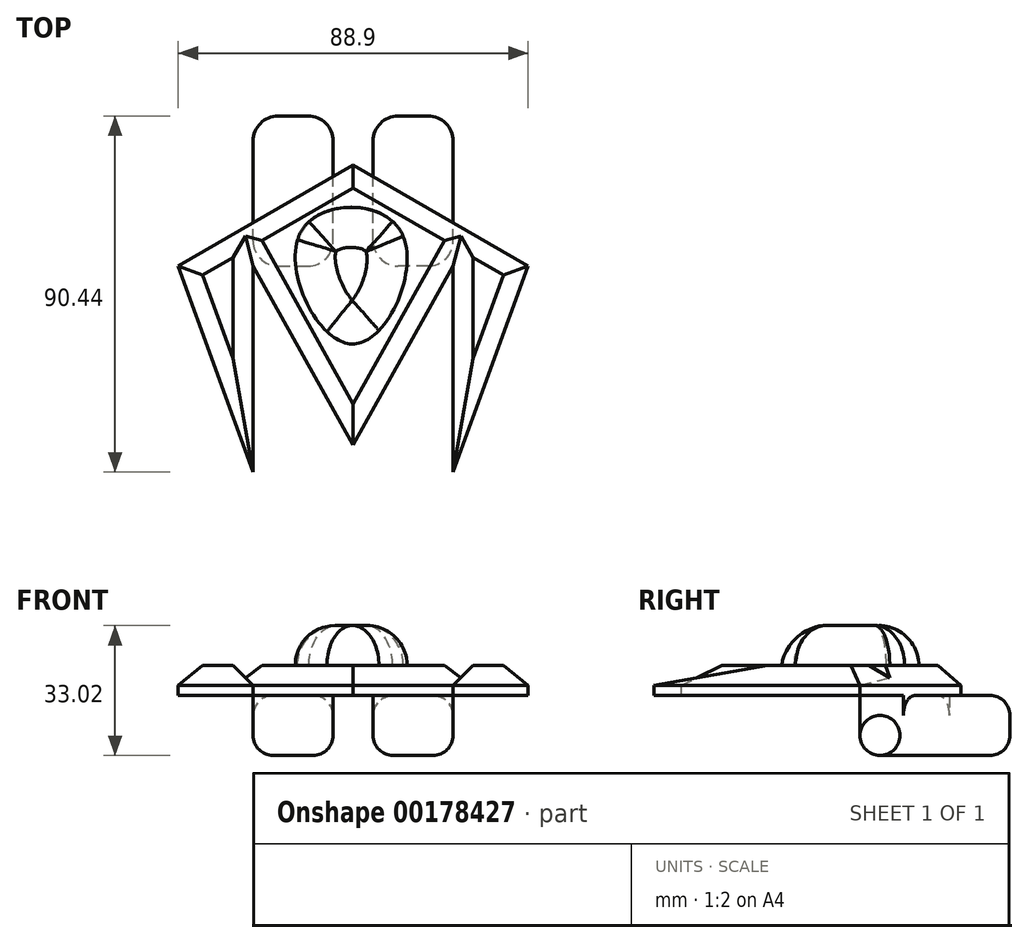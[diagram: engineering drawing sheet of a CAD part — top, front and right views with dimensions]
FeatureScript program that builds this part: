
annotation { "Feature Type Name" : "Feature", "Feature Type Description" : "" }
export const myFeature = defineFeature(function(context is Context, id is Id, definition is map)
    precondition{}
    {
        {
            var Q0;
            Q0=qCreatedBy(makeId("Top.planeOp"),FACE);
            var sketch = newSketch(context, id + "F0", { "sketchPlane" : qUnion([Q0])});
            skLineSegment(sketch, "E0", {"start": v(-25.4, 8.08) * mm, "end": v(0, -37.38) * mm});
            skLineSegment(sketch, "E1", {"start": v(0, -37.38) * mm, "end": v(25.4, 8.08) * mm});
            skLineSegment(sketch, "E2", {"start": v(25.4, 8.08) * mm, "end": v(25.4, -44.26) * mm});
            skLineSegment(sketch, "E3", {"start": v(-25.4, 8.08) * mm, "end": v(-25.4, -44.26) * mm});
            skLineSegment(sketch, "E4", {"start": v(-25.4, -44.26) * mm, "end": v(-44.45, 8.08) * mm});
            skLineSegment(sketch, "E5", {"start": v(25.4, -44.26) * mm, "end": v(44.45, 8.08) * mm});
            skLineSegment(sketch, "E6", {"start": v(0, -37.38) * mm, "end": v(0, 33.74) * mm});
            skLineSegment(sketch, "E7", {"start": v(0, 33.74) * mm, "end": v(44.45, 8.08) * mm});
            skLineSegment(sketch, "E8", {"start": v(0, 33.74) * mm, "end": v(-44.45, 8.08) * mm});
            skSolve(sketch);
        }
        {
            var Q0;
            Q0 = qSketchRegion(id + "F0", true);
            extrude(context, id + "F1", {"entities" : qUnion([Q0]), "depth" : 7.62 * mm});
        }
        {
            var Q0;
            Q0=makeQuery(id+"F1.opExtrude","CAP_FACE",FACE,{"disambiguationData":[OSD([sQuery(id+"F0.wireOp",EDGE,"E0"),sQuery(id+"F0.wireOp",EDGE,"E1"),sQuery(id+"F0.wireOp",EDGE,"E2"),sQuery(id+"F0.wireOp",EDGE,"E3"),sQuery(id+"F0.wireOp",EDGE,"E4"),sQuery(id+"F0.wireOp",EDGE,"E5"),sQuery(id+"F0.wireOp",EDGE,"E7"),sQuery(id+"F0.wireOp",EDGE,"E8")])],"isStart":false});
            chamfer(context, id + "F2", {"entities" : qUnion([Q0]), "width" : 5.08 * mm, "tangentPropagation" : true});
        }
        {
            var Q0;
            Q0=makeQuery(id+"F1.opExtrude","CAP_FACE",FACE,{"disambiguationData":[OSD([sQuery(id+"F0.wireOp",EDGE,"E0"),sQuery(id+"F0.wireOp",EDGE,"E1"),sQuery(id+"F0.wireOp",EDGE,"E2"),sQuery(id+"F0.wireOp",EDGE,"E3"),sQuery(id+"F0.wireOp",EDGE,"E4"),sQuery(id+"F0.wireOp",EDGE,"E5"),sQuery(id+"F0.wireOp",EDGE,"E7"),sQuery(id+"F0.wireOp",EDGE,"E8")])],"isStart":true});
            var sketch = newSketch(context, id + "F3", { "sketchPlane" : qUnion([Q0])});
            skLineSegment(sketch, "E9.bottom", {"start": v(-19.05, -8.08) * mm, "end": v(-11.43, -8.08) * mm});
            skLineSegment(sketch, "E9.top", {"start": v(-19.05, -46.18) * mm, "end": v(-11.43, -46.18) * mm});
            skLineSegment(sketch, "E9.left", {"start": v(-25.4, -14.43) * mm, "end": v(-25.4, -39.83) * mm});
            skLineSegment(sketch, "E9.right", {"start": v(-5.08, -14.43) * mm, "end": v(-5.08, -39.83) * mm});
            skLineSegment(sketch, "E10.bottom", {"start": v(19.05, -8.08) * mm, "end": v(11.43, -8.08) * mm});
            skLineSegment(sketch, "E10.top", {"start": v(19.05, -46.18) * mm, "end": v(11.43, -46.18) * mm});
            skLineSegment(sketch, "E10.left", {"start": v(25.4, -14.43) * mm, "end": v(25.4, -39.83) * mm});
            skLineSegment(sketch, "E10.right", {"start": v(5.08, -14.43) * mm, "end": v(5.08, -39.83) * mm});
            skPoint(sketch, "E11.visualSharp", {"position": v(-25.4, -8.08) * mm});
            skArc(sketch, "E11.filletArc", {"start": v(-19.05, -8.08) * mm, "mid": v(-23.54, -9.94) * mm, "end": v(-25.4, -14.43) * mm});
            skPoint(sketch, "E12.visualSharp", {"position": v(-5.08, -8.08) * mm});
            skArc(sketch, "E12.filletArc", {"start": v(-5.08, -14.43) * mm, "mid": v(-6.94, -9.94) * mm, "end": v(-11.43, -8.08) * mm});
            skPoint(sketch, "E13.visualSharp", {"position": v(-5.08, -46.18) * mm});
            skArc(sketch, "E13.filletArc", {"start": v(-11.43, -46.18) * mm, "mid": v(-6.94, -44.32) * mm, "end": v(-5.08, -39.83) * mm});
            skPoint(sketch, "E14.visualSharp", {"position": v(-25.4, -46.18) * mm});
            skArc(sketch, "E14.filletArc", {"start": v(-25.4, -39.83) * mm, "mid": v(-23.54, -44.32) * mm, "end": v(-19.05, -46.18) * mm});
            skPoint(sketch, "E15.visualSharp", {"position": v(5.08, -46.18) * mm});
            skArc(sketch, "E15.filletArc", {"start": v(5.08, -39.83) * mm, "mid": v(6.94, -44.32) * mm, "end": v(11.43, -46.18) * mm});
            skPoint(sketch, "E16.visualSharp", {"position": v(25.4, -46.18) * mm});
            skArc(sketch, "E16.filletArc", {"start": v(19.05, -46.18) * mm, "mid": v(23.54, -44.32) * mm, "end": v(25.4, -39.83) * mm});
            skPoint(sketch, "E17.visualSharp", {"position": v(25.4, -8.08) * mm});
            skArc(sketch, "E17.filletArc", {"start": v(25.4, -14.43) * mm, "mid": v(23.54, -9.94) * mm, "end": v(19.05, -8.08) * mm});
            skPoint(sketch, "E18.visualSharp", {"position": v(5.08, -8.08) * mm});
            skArc(sketch, "E18.filletArc", {"start": v(11.43, -8.08) * mm, "mid": v(6.94, -9.94) * mm, "end": v(5.08, -14.43) * mm});
            skSolve(sketch);
        }
        {
            var Q0;
            Q0 = qSketchRegion(id + "F3", true);
            extrude(context, id + "F4", {"entities" : qUnion([Q0]), "operationType" : NewBodyOperationType.ADD, "depth" : 15.24 * mm});
        }
        {
            var Q0;
            Q0=makeQuery(id+"F4.opExtrude","SWEPT_FACE",FACE,{"disambiguationData":[OSD([sQuery(id+"F3.wireOp",EDGE,"E10.top")])]});
            var Q1;
            Q1=makeQuery(id+"F4.opExtrude","SWEPT_FACE",FACE,{"disambiguationData":[OSD([sQuery(id+"F3.wireOp",EDGE,"E9.top")])]});
            fillet(context, id + "F5", {"entities" : qUnion([Q0, Q1]), "radius" : 5.08 * mm, "tangentPropagation" : true, "allowEdgeOverflow" : false});
        }
        {
            var Q0;
            Q0=makeQuery(id+"F2.opChamfer","SPLIT",FACE,{"disambiguationData":[OD(2.0)],"derivedFrom":makeQuery(id+"F1.opExtrude","CAP_FACE",FACE,{"disambiguationData":[OSD([sQuery(id+"F0.wireOp",EDGE,"E0"),sQuery(id+"F0.wireOp",EDGE,"E1"),sQuery(id+"F0.wireOp",EDGE,"E2"),sQuery(id+"F0.wireOp",EDGE,"E3"),sQuery(id+"F0.wireOp",EDGE,"E4"),sQuery(id+"F0.wireOp",EDGE,"E5"),sQuery(id+"F0.wireOp",EDGE,"E7"),sQuery(id+"F0.wireOp",EDGE,"E8")])],"isStart":false})});
            var sketch = newSketch(context, id + "F6", { "sketchPlane" : qUnion([Q0])});
            skFitSpline(sketch, "E19", {"points": [v(0, -11.72) * mm, v(-13.35, 16.61) * mm, v(12.05, 16.96) * mm, v(0, -11.72) * mm]});
            skSolve(sketch);
        }
        {
            var Q0;
            Q0 = qSketchRegion(id + "F6", true);
            extrude(context, id + "F7", {"entities" : qUnion([Q0]), "operationType" : NewBodyOperationType.ADD, "depth" : 10.16 * mm});
        }
        {
            var Q0;
            Q0=makeQuery(id+"F7.opExtrude","CAP_FACE",FACE,{"disambiguationData":[OSD([sQuery(id+"F6.wireOp",EDGE,"E19")])],"isStart":false});
            fillet(context, id + "F8", {"entities" : qUnion([Q0]), "radius" : 10.16 * mm, "tangentPropagation" : true, "allowEdgeOverflow" : false});
        }
    });
